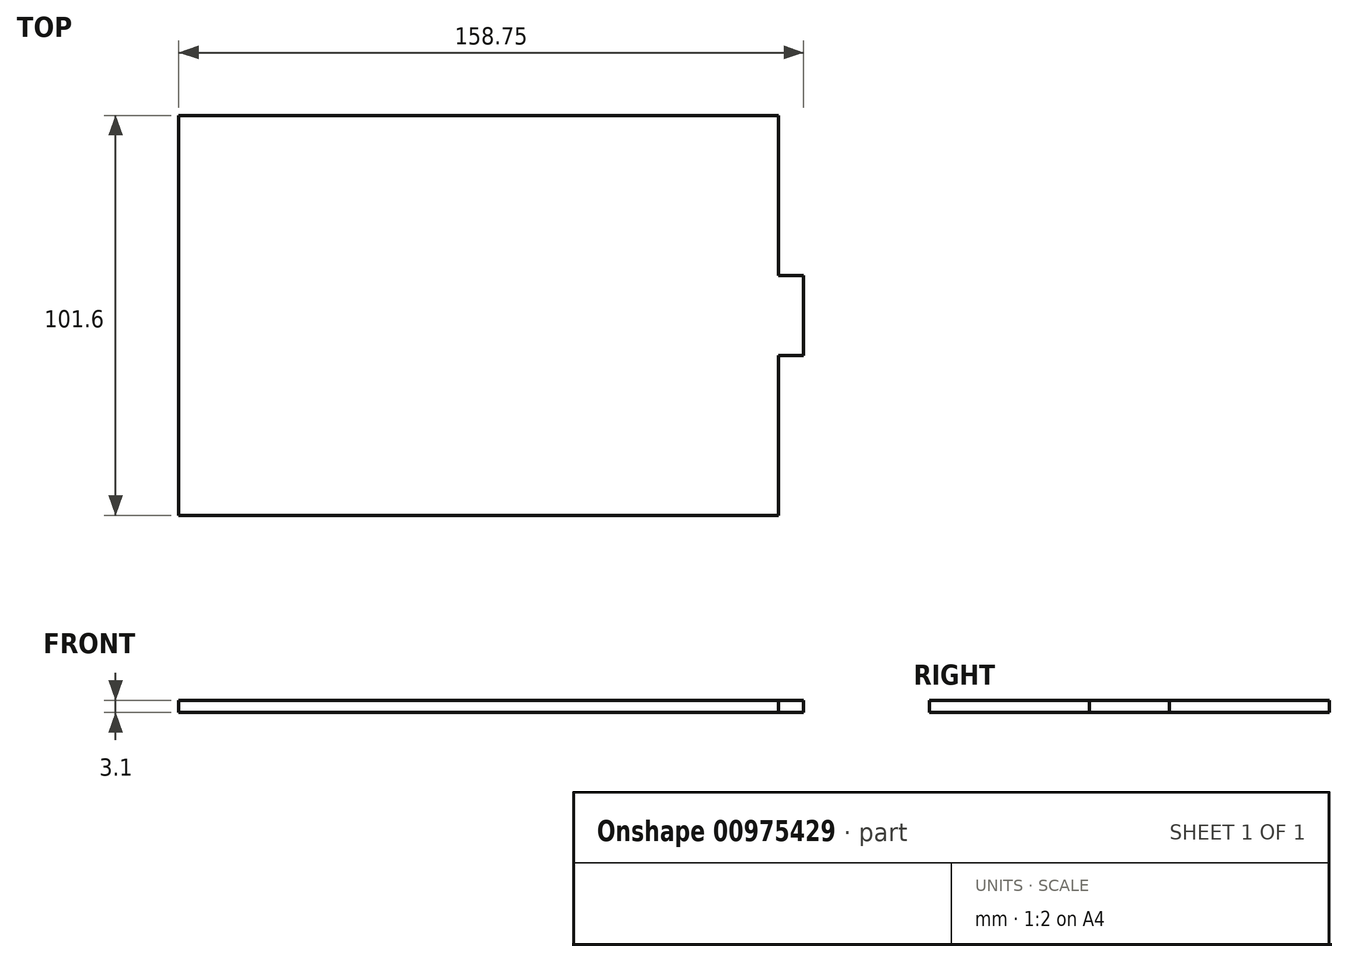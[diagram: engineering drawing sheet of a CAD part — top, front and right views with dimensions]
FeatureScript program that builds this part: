
annotation { "Feature Type Name" : "Feature", "Feature Type Description" : "" }
export const myFeature = defineFeature(function(context is Context, id is Id, definition is map)
    precondition{}
    {
        {
            var Q0;
            Q0=qCreatedBy(makeId("Top.planeOp"),FACE);
            var sketch = newSketch(context, id + "F0", { "sketchPlane" : qUnion([Q0])});
            skLineSegment(sketch, "E0.bottom", {"start": v(0, 0) * mm, "end": v(152.4, 0) * mm});
            skLineSegment(sketch, "E0.top", {"start": v(0, 101.6) * mm, "end": v(152.4, 101.6) * mm});
            skLineSegment(sketch, "E0.left", {"start": v(0, 0) * mm, "end": v(0, 101.6) * mm});
            skLineSegment(sketch, "E0.right", {"start": v(152.4, 0) * mm, "end": v(152.4, 101.6) * mm});
            skLineSegment(sketch, "E1.bottom", {"start": v(152.4, 60.96) * mm, "end": v(158.75, 60.96) * mm});
            skLineSegment(sketch, "E1.top", {"start": v(152.4, 40.64) * mm, "end": v(158.75, 40.64) * mm});
            skLineSegment(sketch, "E1.left", {"start": v(152.4, 60.96) * mm, "end": v(152.4, 40.64) * mm});
            skLineSegment(sketch, "E1.right", {"start": v(158.75, 60.96) * mm, "end": v(158.75, 40.64) * mm});
            skLineSegment(sketch, "E2", {"start": v(152.4, 50.8) * mm, "end": v(127.68, 50.8) * mm, "construction": true});
            skSolve(sketch);
        }
        {
            var Q0;
            Q0=makeQuery(id+"F0.imprint","IMPRINT",FACE,{"disambiguationData":[TD([[makeQuery(id+"F0.imprint","IMPRINT",EDGE,{"derivedFrom":sQuery(id+"F0.wireOp",EDGE,"E0.bottom")}),1.0]])]});
            var Q1;
            Q1=makeQuery(id+"F0.imprint","IMPRINT",FACE,{"disambiguationData":[TD([[makeQuery(id+"F0.imprint","IMPRINT",EDGE,{"derivedFrom":sQuery(id+"F0.wireOp",EDGE,"E1.bottom")}),-1.0]])]});
            extrude(context, id + "F1", {"entities" : qUnion([Q0, Q1]), "depth" : 3.1 * mm, "offsetDistance" : 25.4 * mm});
        }
    });
